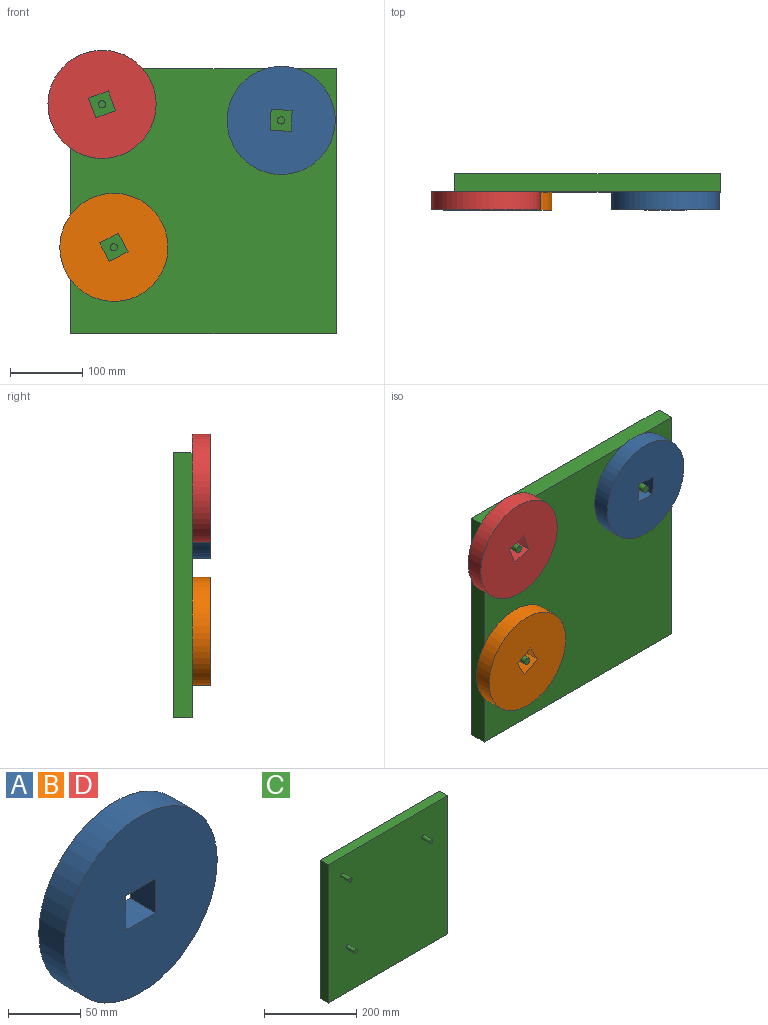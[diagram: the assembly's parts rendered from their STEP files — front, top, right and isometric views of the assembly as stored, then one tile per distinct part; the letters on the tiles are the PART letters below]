
ASSEMBLY  parts=4 mates=3
PART A: 7 faces, bbox 150x25x150 mm
  f0: plane 29.1x25mm, normal (-1,0,0), area 727.5mm2, adj f1,f3,f5,f6
  f1: plane 29.1x25mm, normal (0,0,1), area 727.5mm2, adj f0,f2,f5,f6
  f2: plane 29.1x25mm, normal (1,0,0), area 727.5mm2, adj f1,f3,f5,f6
  f3: plane 29.1x25mm, normal (0,0,-1), area 727.5mm2, adj f0,f2,f5,f6
  f4: cylinder r=75mm len=150mm, axis (0,1,0), area 11781mm2, adj f5,f6
  f5: plane 150x150mm, normal (0,-1,0), area 16824.7mm2, adj f0,f1,f2,f3,f4
  f6: plane 150x150mm, normal (0,1,0), area 16824.7mm2, adj f0,f1,f2,f3,f4
PART B: same geometry as A
PART C: 12 faces, bbox 367.6x50x367.6 mm
  f0: plane 367.62x25mm, normal (0,0,-1), area 9190.5mm2, adj f1,f3,f4,f5
  f1: plane 367.62x25mm, normal (1,0,0), area 9190.5mm2, adj f0,f2,f4,f5
  f2: plane 367.62x25mm, normal (0,0,1), area 9190.5mm2, adj f1,f3,f4,f5
  f3: plane 367.62x25mm, normal (-1,0,0), area 9190.5mm2, adj f0,f2,f4,f5
  f4: plane 367.62x367.62mm, normal (0,-1,0), area 134908.5mm2, adj f0,f1,f2,f3,f6,f8,f10
  f5: plane 367.62x367.62mm, normal (0,1,0), area 135144.2mm2, adj f0,f1,f2,f3
  f6: cylinder r=5mm len=25mm, axis (0,1,0), area 785.4mm2, adj f4,f7
  f7: plane 10x10mm, normal (0,-1,0), area 78.5mm2, adj f6
  f8: cylinder r=5mm len=25mm, axis (0,1,0), area 785.4mm2, adj f4,f9
  f9: plane 10x10mm, normal (0,-1,0), area 78.5mm2, adj f8
  f10: cylinder r=5mm len=25mm, axis (0,1,0), area 785.4mm2, adj f4,f11
  f11: plane 10x10mm, normal (0,-1,0), area 78.5mm2, adj f10
PART D: same geometry as A
PLACE A rot(axis=(0,-1,0),87.4deg) t=(-51.49,-9.26,-385.41)mm
PLACE B rot(axis=(0,1,0),152.3deg) t=(-13.3,-9.26,-7)mm
PLACE C t=(-183.22,-9.26,-142.59)mm fixed
PLACE D rot(axis=(0,1,0),70deg) t=(-482.56,-9.26,309.79)mm
MATE revolute D.f4 <-> C.f6  axis (0,1,0) through (-323.93,-34.26,-8.43)mm
MATE revolute A.f4 <-> C.f8  axis (0,1,0) through (-75.53,-34.26,-30.66)mm
MATE revolute B.f4 <-> C.f10  axis (0,1,0) through (-307.49,-34.26,-206.69)mm
